# Revit family: 2CKA006410A0379
name_source: partatom
category: Elektroinstallationen
revit_build: Autodesk Revit 2017 (Build: 20160225_1515(x64)
units: mm (PartAtom-declared; Revit-internal decimal feet)

## family parameters
Basisbauteil = Fläche
Beim Laden mit Abzugskörper schneiden = Nein
Bemaßung runder Anschluss = Durchmesser verwenden
Beschriftungsausrichtung beibehalten = Nein
Gemeinsam genutzt = Nein
Raumberechnungspunkt = Nein
Teiletyp = Normal

## types (1)
- 2CKA006410A0379
    Ausführung der Oberfläche = glänzend
    Aussperrsicherung = Ja
    BIM = https://media.live.bim.site
    BIMSITE_PRODUCT_ID = 2cf7ad59a4c21524e7fba2feec5df99f6db13eb7
    Befestigungsart = Krallen-/Schraubbefestigung
    Beschreibung = Busch-Jalousiecontrol II-Einsatz, UP-Montagedosen und -Einsätze, Einsätze für Jalousiesteuerung/Zeitschaltuhren, Busch-Jalousiecontrol II-Einsatz Geeignet für Rollladen-, Jalousie- und Markisenantriebe mit mechanischer oder elektronischer Endlagenabschaltung. Mit zwei 230 V-Nebenstelleneingängen (Auf/Ab) für Gruppensteuerung. Anschlussmöglichkeit von Helligkeitssensor 6414-101 und Glasbruchmelder 6413. Mit Betriebsartenschalter für Betriebsarten: Normal, Lamelle, Zentrale, Position, Markise. Mit Party-Funktion (Deaktivierung der Vorort-Bedienstelle) in Kombination mit Busch-Jalousiecontrol II Bedienelement 6430-xx-xxx, 6066-xx-xxx. Windalarm-, Putz-Funktion über Nebenstelleneingang realisierbar. Für Bedienelement 6430-xx-xxx. Für IR-Bedienelement 6066-xx-xxx. Für Komfort-Timer-Bedienelement 6455-101. Laufzeit: 3 min Nennspannung: , +10 % / -10 % Nennfrequenz: 50 Hz Ausgänge: 2x Schließer Nennstrom: 3 A, bei cos ? 0,5 Nennleistung: 690 VA Steuer-/Signalausgänge: 2 Temperaturbereich Gerät: 0 °C bis 35 °C
    Datenblatt = https://media.live.bim.site
    Farbe = schwarz
    Frequenz [Hz] = [50:50]
    GTIN = 4011395076514
    Geeignet für Schutzart (IP) = IP20
    Gerätebreite [mm] = 71
    Gerätehöhe [mm] = 71
    Gerätetiefe [mm] = 33
    Gewicht [kg/m] = 0.089
    HAN = 2CKA006410A0379
    Halogenfrei = Ja
    HeinzeBIM = https://www.heinze.de
    Hersteller = Busch-Jaeger
    Ist System = Nein
    Ist Zubehör = Nein
    Max. Schaltleistung [Voltampere] = 690
    Mit Glasbruchmelderanschluss = Ja
    Mit Helligkeitssensoranschluss = Ja
    Montageart = Unterputz
    Nebenstelleneingang = Ja
    Nennspannung [V] [Volt] = 230
    Oberfläche = unbehandelt
    Produktseite = https://media.live.bim.site
    Sonnenschutzwert einstellbar [lx] = [5000:50000]
    TYPE = 6411 U/S-101
    Typname = Busch-Jalousiecontrol II-Einsatz, UP-Montagedosen und -Einsätze, Einsätze für Jalousiesteuerung/Zeitschaltuhren
    URL = https://www.busch-jaeger.de
    Vorgabe-Ansicht = 1219 mm
    Werkstoff = Kunststoff
    Werkstoffgüte = Thermoplast
    White = White
    Zusammenstellung = Basiselement

## geometry (parser evidence)
native form markers: Sweep x3
no freeform markers — native parametric forms only
